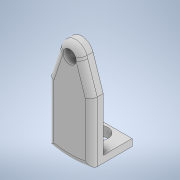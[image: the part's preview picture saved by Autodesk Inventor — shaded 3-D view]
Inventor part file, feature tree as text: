
AUTODESK INVENTOR PART (.ipt)
format: ipt  version: 2022.2 (Build 262287000, 287)  size: 154,624 bytes
history: native  units: mm
features: reference x5, other x4, extrude x3, sketch x3, plane x1, fillet x1, projected_geometry x1
ambient origin geometry x8: Origin, YZ Plane, XZ Plane, XY Plane, X Axis, Y Axis, Z Axis, Center Point
bodies: Solid1 (feature_tree)
feature tree (18):
  extrude  "Extrusion1"  Depth=1.0mm TaperAngle=0.0deg
  sketch  "Sketch2"  dims[d4=10.0mm d5=0.0mm d6=1.0mm]
  plane  "Work Plane1"
  extrude  "Extrusion2"  Depth=1.0mm
  extrude  "Extrusion3"  [1 undecoded]
  fillet  "Fillet1"  [1 undecoded]
  sketch  "Sketch1"  dims[d0=2.0mm d1=0.0mm d2=1.0mm d3=0.0mm]
  reference  "Reference1"
  reference  "Reference2"
  reference  "Reference4"
  reference  "Reference5"
  projected_geometry  "Projected Loop1"
  sketch  "Sketch3"
  reference  "Reference6"
  other  "<userpath>\Documents\Inventor\Wire Bender\Assembly.iam"
  other  "Assembly.iam"
  other  "Tool Head:1"
  other  "Crank:1"
note: 2 required parameter values undecoded (feature->parameter linkage not recoverable at this tier; creation-order binding heuristic only, values carry confidence <= 0.55)
